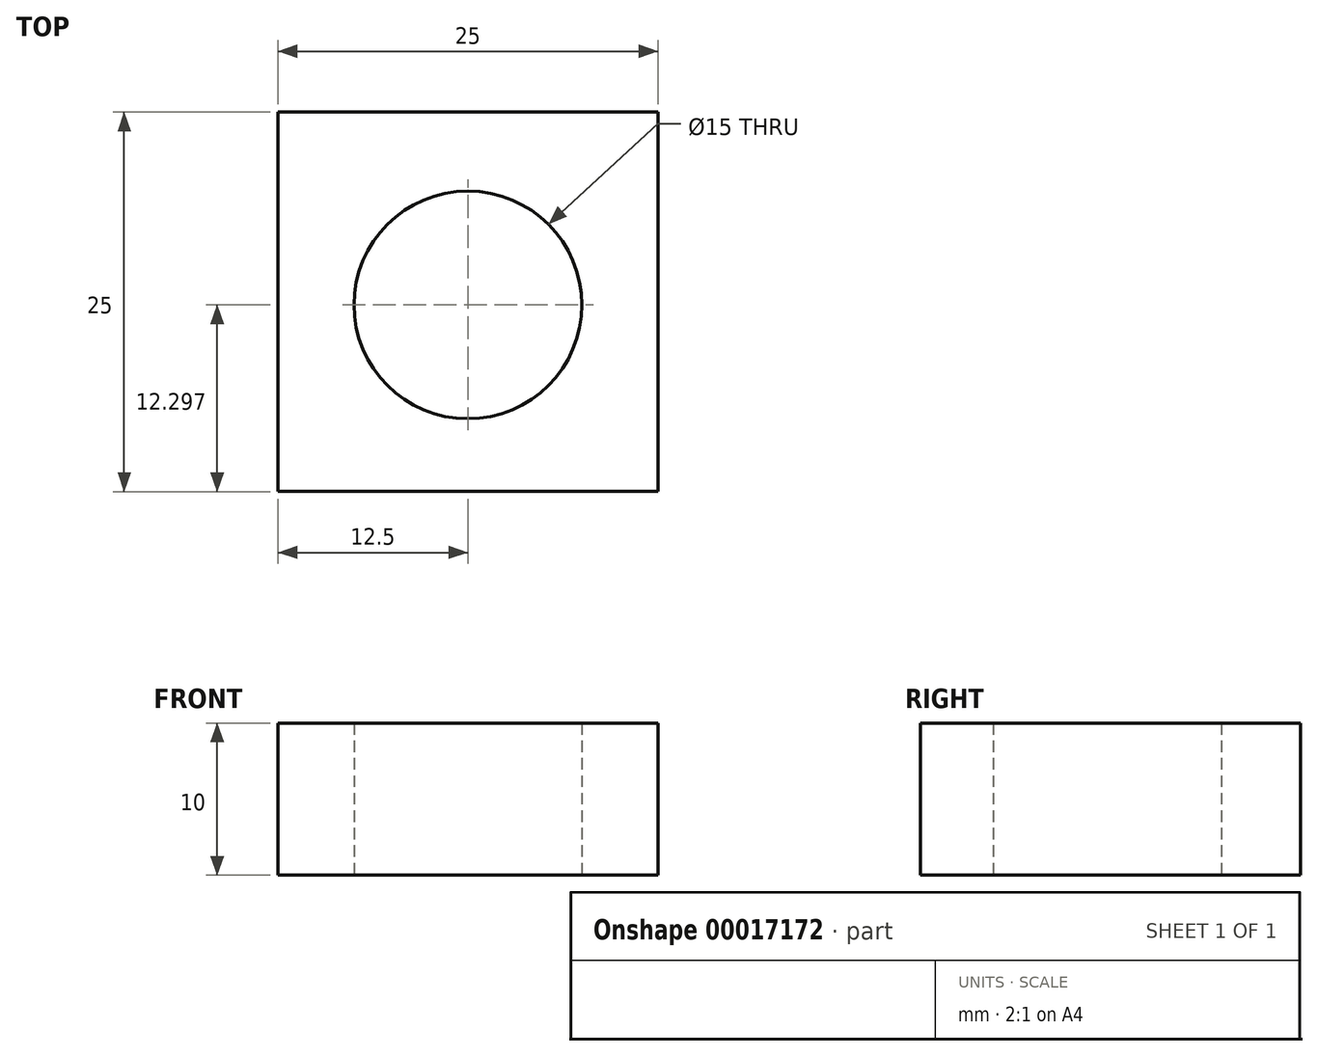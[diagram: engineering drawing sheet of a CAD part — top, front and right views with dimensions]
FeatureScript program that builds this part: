
annotation { "Feature Type Name" : "Feature", "Feature Type Description" : "" }
export const myFeature = defineFeature(function(context is Context, id is Id, definition is map)
    precondition{}
    {
        {
            var Q0;
            Q0=qCreatedBy(makeId("Top.planeOp"),FACE);
            var sketch = newSketch(context, id + "F0", { "sketchPlane" : qUnion([Q0])});
            skLineSegment(sketch, "E0.bottom", {"start": v(-12.5, 17.37) * mm, "end": v(12.5, 17.37) * mm});
            skLineSegment(sketch, "E0.top", {"start": v(-12.5, -7.63) * mm, "end": v(12.5, -7.63) * mm});
            skLineSegment(sketch, "E0.left", {"start": v(-12.5, 17.37) * mm, "end": v(-12.5, -7.63) * mm});
            skLineSegment(sketch, "E0.right", {"start": v(12.5, 17.37) * mm, "end": v(12.5, -7.63) * mm});
            skCircle(sketch, "E1", {"center": v(0, 4.67) * mm, "radius": 7.5 * mm});
            skSolve(sketch);
        }
        {
            var Q0;
            Q0=makeQuery(id+"F0.imprint","IMPRINT",FACE,{"disambiguationData":[TD([[makeQuery(id+"F0.imprint","IMPRINT",EDGE,{"derivedFrom":sQuery(id+"F0.wireOp",EDGE,"E0.bottom")}),-1.0]])]});
            extrude(context, id + "F1", {"entities" : qUnion([Q0]), "depth" : 10 * mm});
        }
    });
